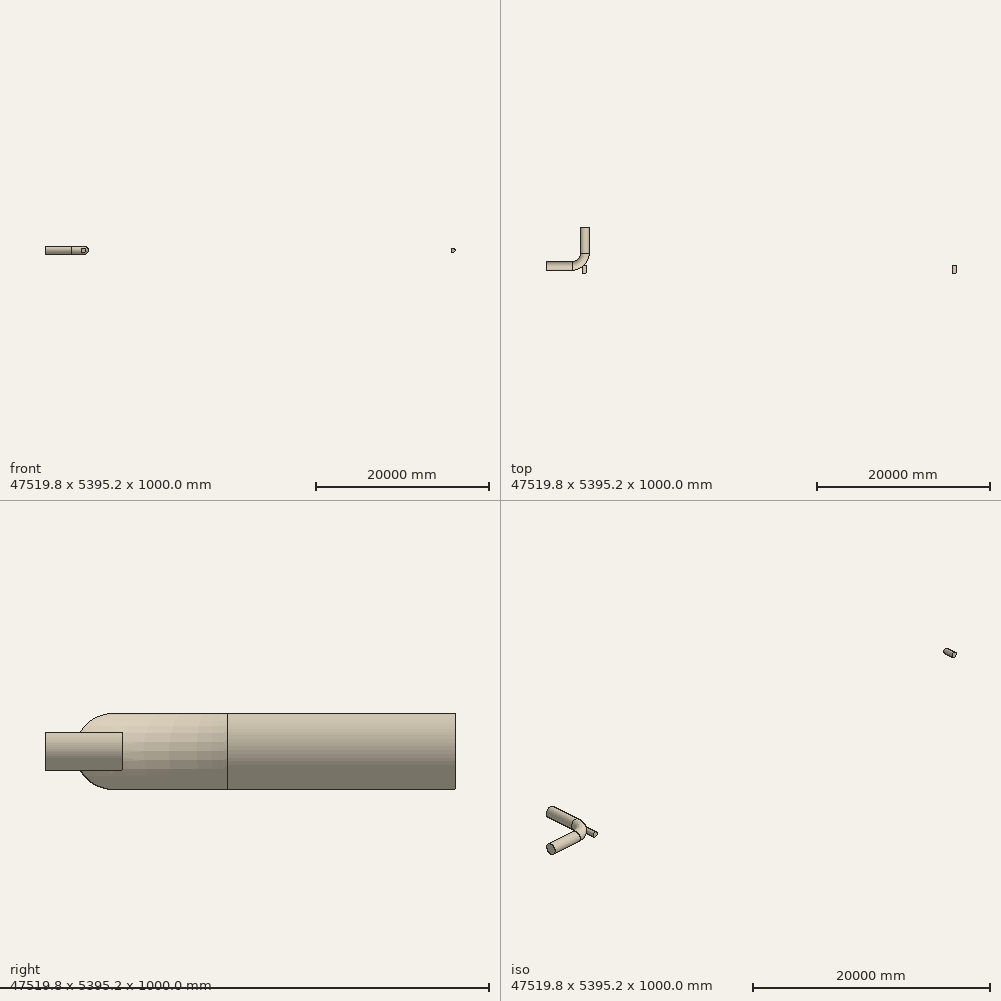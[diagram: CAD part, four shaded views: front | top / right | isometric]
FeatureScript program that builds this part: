
annotation { "Feature Type Name" : "Feature", "Feature Type Description" : "" }
export const myFeature = defineFeature(function(context is Context, id is Id, definition is map)
    precondition{}
    {
        {
            var Q0;
            Q0=qCreatedBy(makeId("Top.planeOp"),FACE);
            var sketch = newSketch(context, id + "F0", { "sketchPlane" : qUnion([Q0])});
            skLineSegment(sketch, "E0", {"start": v(0, 0) * mm, "end": v(3000, 0) * mm});
            skLineSegment(sketch, "E1", {"start": v(4459.3, 1500) * mm, "end": v(4459.3, 4500) * mm});
            skArc(sketch, "E2", {"start": v(4459.3, 1500) * mm, "mid": v(4034.44, 453.48) * mm, "end": v(3000, 0) * mm});
            skLineSegment(sketch, "E3", {"start": v(2959.3, 1499.45) * mm, "end": v(4459.3, 1500) * mm});
            skArc(sketch, "E4.0", {"start": v(4959.3, 1500.18) * mm, "mid": v(4392.82, 104.82) * mm, "end": v(3013.57, -499.82) * mm});
            skPoint(sketch, "E5.startSnap0", {"position": v(4392.82, 104.82) * mm});
            skLineSegment(sketch, "E6", {"start": v(4392.82, 104.82) * mm, "end": v(4392.82, -895.18) * mm});
            skSolve(sketch);
        }
        {
            var Q0;
            Q0=qCreatedBy(makeId("Right.planeOp"),FACE);
            var sketch = newSketch(context, id + "F1", { "sketchPlane" : qUnion([Q0])});
            skCircle(sketch, "E7", {"center": v(0, 0) * mm, "radius": 500 * mm});
            skSolve(sketch);
        }
        {
            var Q0;
            Q0=makeQuery(id+"F1.imprint","IMPRINT",FACE,{"disambiguationData":[TD([[makeQuery(id+"F1.imprint","IMPRINT",EDGE,{"derivedFrom":sQuery(id+"F1.wireOp",EDGE,"E7")}),1.0]])]});
            var Q1;
            Q1=sQuery(id+"F0.wireOp",EDGE,"E0");
            var Q2;
            Q2=sQuery(id+"F0.wireOp",EDGE,"E2");
            var Q3;
            Q3=sQuery(id+"F0.wireOp",EDGE,"E1");
            sweep(context, id + "F2", {"profiles" : qUnion([Q0]), "path" : qUnion([Q1, Q2, Q3])});
        }
        {
            var Q0;
            Q0=sQuery(id+"F0.wireOp",VERTEX,"E6.end");
            var Q1;
            Q1=sQuery(id+"F0.wireOp",EDGE,"E6");
            cPlane(context, id + "F3", {"entities" : qUnion([Q0, Q1]), "cplaneType" : CPlaneType.LINE_POINT, "offset" : 25 * mm, "width" : 150 * mm, "height" : 150 * mm});
        }
        {
            var Q0;
            Q0=qCreatedBy(id+"F3.planeOp",FACE);
            var sketch = newSketch(context, id + "F4", { "sketchPlane" : qUnion([Q0])});
            skCircle(sketch, "E8", {"center": v(47269.81, 0) * mm, "radius": 250 * mm});
            skCircle(sketch, "E9", {"center": v(4400.7, 0) * mm, "radius": 250 * mm});
            skSolve(sketch);
        }
        {
            var Q0;
            Q0 = qSketchRegion(id + "F4", true);
            extrude(context, id + "F5", {"entities" : qUnion([Q0]), "operationType" : NewBodyOperationType.ADD, "oppositeDirection" : true, "depth" : 1009 * mm, "offsetDistance" : 25 * mm});
        }
    });
